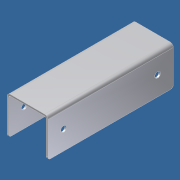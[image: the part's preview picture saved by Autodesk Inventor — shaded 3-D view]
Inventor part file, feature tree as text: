
AUTODESK INVENTOR PART (.ipt)
format: ipt  version: 2012 (Build 160160000, 160)  size: 110,080 bytes
history: native  units: in
note: dims shown in document units (in); Inventor stores cm internally (conversion verified against a paired STEP export)
features: extrude x1, fillet x1, hole x1, pattern_linear x1, sketch x1
ambient origin geometry x8: Origin, YZ Plane, XZ Plane, XY Plane, X Axis, Y Axis, Z Axis, Center Point
bodies: Solid1 (feature_tree)
feature tree (5):
  extrude  "Extrusion1"  Depth=1.83in
  fillet  "Fillet1"  Radius=6.0in
  hole  "Hole1"  [1 undecoded]
  pattern_linear  "Rectangular Pattern1"  Spacing1=0.08in  [1 undecoded]
  sketch  "Sketch1"  dims[d1=0.078in d3=1.83in d4=6.0in d5=0.0in d6=1.8in d7=0.08in d8=0.125in d9=0.75in d10=0.915in d11=0.275in d12=0.75in d13=0.375in d14=0.25in d15=0.5635in d16=1.0in d17=0.8108in d18=0.7874in d20=4.5in]
note: 2 required parameter values undecoded (feature->parameter linkage not recoverable at this tier; creation-order binding heuristic only, values carry confidence <= 0.55)
